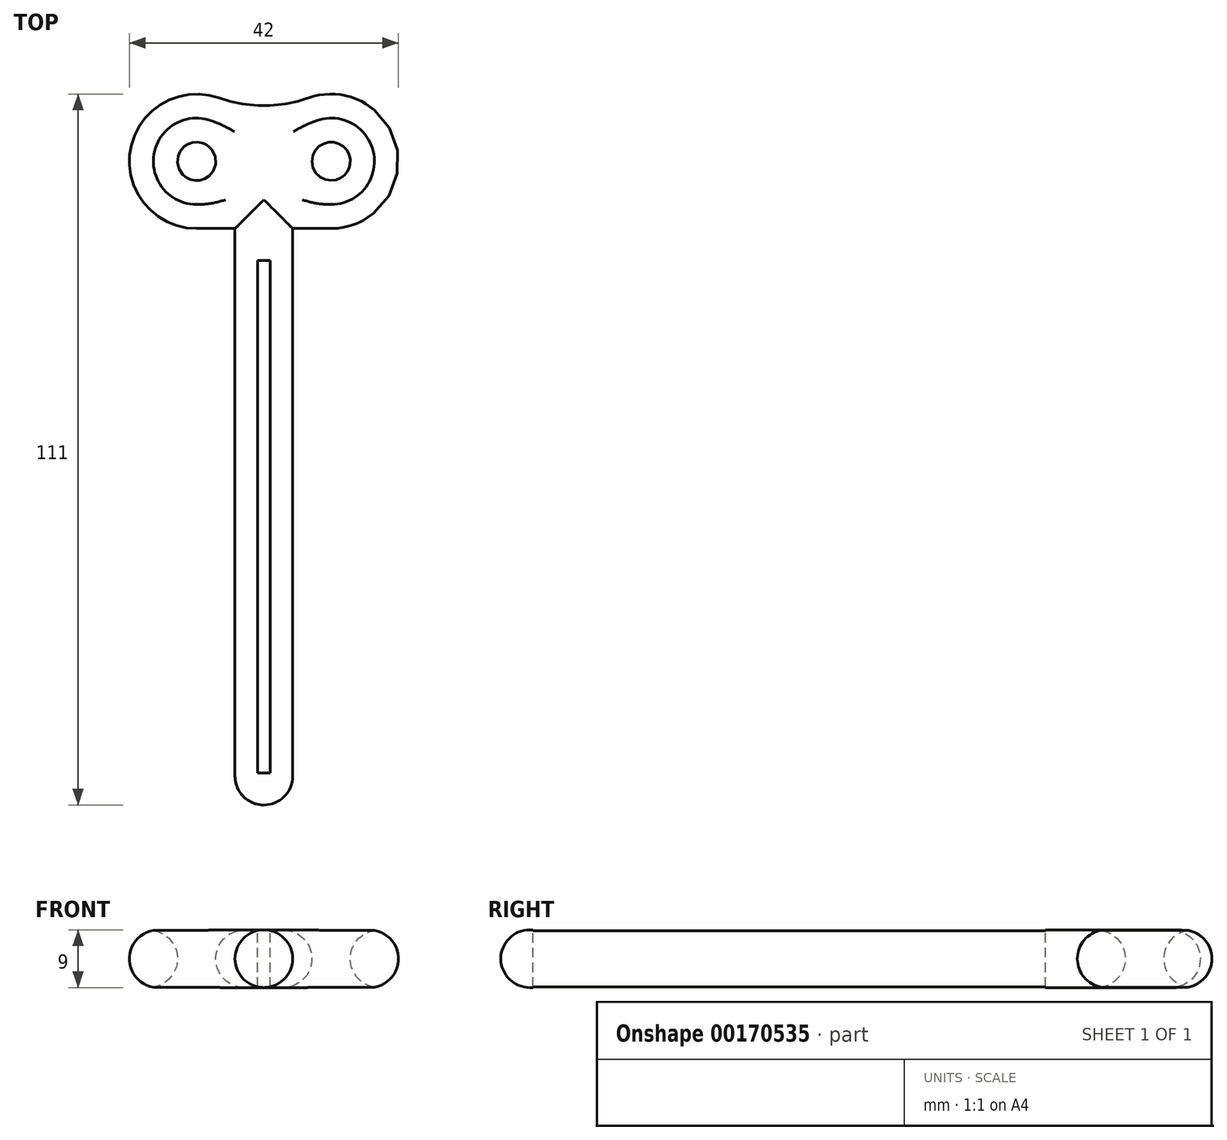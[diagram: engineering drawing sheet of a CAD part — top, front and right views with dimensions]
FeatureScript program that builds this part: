
annotation { "Feature Type Name" : "Feature", "Feature Type Description" : "" }
export const myFeature = defineFeature(function(context is Context, id is Id, definition is map)
    precondition{}
    {
        {
            var Q0;
            Q0=qCreatedBy(makeId("Top.planeOp"),FACE);
            var sketch = newSketch(context, id + "F0", { "sketchPlane" : qUnion([Q0])});
            skLineSegment(sketch, "E0", {"start": v(-4.5, 4.5) * mm, "end": v(-4.5, 90) * mm});
            skLineSegment(sketch, "E1", {"start": v(0, 0) * mm, "end": v(0, 45.82) * mm, "construction": true});
            skArc(sketch, "E2", {"start": v(-4.5, 4.5) * mm, "mid": v(-3.18, 1.32) * mm, "end": v(0, 0) * mm});
            skLineSegment(sketch, "E3", {"start": v(-4.5, 90) * mm, "end": v(0, 90) * mm});
            skLineSegment(sketch, "E4", {"start": v(0, 90) * mm, "end": v(0, 0) * mm});
            skSolve(sketch);
        }
        {
            var Q0;
            Q0=makeQuery(id+"F0.imprint","IMPRINT",FACE,{"disambiguationData":[TD([[makeQuery(id+"F0.imprint","IMPRINT",EDGE,{"derivedFrom":sQuery(id+"F0.wireOp",EDGE,"E0")}),-1.0]])]});
            var Q1;
            Q1=sQuery(id+"F0.wireOp",EDGE,"E4");
            revolve(context, id + "F1", {"entities" : qUnion([Q0]), "axis" : qUnion([Q1]), "revolveType" : RevolveType.FULL});
        }
        {
            var Q0;
            Q0=qCreatedBy(makeId("Top.planeOp"),FACE);
            var sketch = newSketch(context, id + "F2", { "sketchPlane" : qUnion([Q0])});
            skLineSegment(sketch, "E5", {"start": v(-10.5, 100.5) * mm, "end": v(10.5, 100.5) * mm, "construction": true});
            skCircle(sketch, "E6", {"center": v(10.5, 100.5) * mm, "radius": 10.5 * mm});
            skCircle(sketch, "E7", {"center": v(-10.5, 100.5) * mm, "radius": 10.5 * mm});
            skCircle(sketch, "E8", {"center": v(-10.5, 100.5) * mm, "radius": 3 * mm});
            skCircle(sketch, "E9", {"center": v(10.5, 100.5) * mm, "radius": 3 * mm});
            skLineSegment(sketch, "E10", {"start": v(-10.5, 90) * mm, "end": v(10.5, 90) * mm});
            skArc(sketch, "E11", {"start": v(-7, 110.4) * mm, "mid": v(0, 109.2) * mm, "end": v(7, 110.4) * mm});
            skLineSegment(sketch, "E12.bottom", {"start": v(-1, 85) * mm, "end": v(1, 85) * mm});
            skLineSegment(sketch, "E12.top", {"start": v(-1, 5) * mm, "end": v(1, 5) * mm});
            skLineSegment(sketch, "E12.left", {"start": v(-1, 85) * mm, "end": v(-1, 5) * mm});
            skLineSegment(sketch, "E12.right", {"start": v(1, 85) * mm, "end": v(1, 5) * mm});
            skSolve(sketch);
        }
        {
            var Q0;
            Q0=makeQuery(id+"F2.imprint","IMPRINT",FACE,{"disambiguationData":[TD([[makeQuery(id+"F2.imprint","IMPRINT",EDGE,{"derivedFrom":sQuery(id+"F2.wireOp",EDGE,"E8")}),-1.0]])]});
            var Q1;
            {var subQ0=sQuery(id+"F2.wireOp",EDGE,"E10");Q1=makeQuery(id+"F2.imprint","IMPRINT",FACE,{"disambiguationData":[TD([[makeQuery(id+"F2.imprint","IMPRINT",EDGE,{"derivedFrom":subQ0}),1.0]])]});}
            var Q2;
            Q2=makeQuery(id+"F2.imprint","IMPRINT",FACE,{"disambiguationData":[TD([[makeQuery(id+"F2.imprint","IMPRINT",EDGE,{"derivedFrom":sQuery(id+"F2.wireOp",EDGE,"E9")}),-1.0]])]});
            var Q3;
            {var subQ0=sQuery(id+"F2.wireOp",EDGE,"E11");Q3=makeQuery(id+"F2.imprint","IMPRINT",FACE,{"disambiguationData":[TD([[makeQuery(id+"F2.imprint","IMPRINT",EDGE,{"derivedFrom":subQ0}),-1.0]])]});}
            extrude(context, id + "F3", {"entities" : qUnion([Q0, Q1, Q2, Q3]), "operationType" : NewBodyOperationType.ADD, "endBound" : BoundingType.SYMMETRIC, "depth" : 9 * mm});
        }
        {
            var Q0;
            Q0=makeQuery(id+"F2.imprint","IMPRINT",FACE,{"disambiguationData":[TD([[makeQuery(id+"F2.imprint","IMPRINT",EDGE,{"derivedFrom":sQuery(id+"F2.wireOp",EDGE,"E12.bottom")}),-1.0]])]});
            extrude(context, id + "F4", {"entities" : qUnion([Q0]), "operationType" : NewBodyOperationType.REMOVE, "endBound" : BoundingType.SYMMETRIC, "oppositeDirection" : true, "depth" : 25 * mm});
        }
        {
            var Q0;
            Q0=makeQuery(id+"F3.opExtrude","CAP_FACE",FACE,{"disambiguationData":[OSD([sQuery(id+"F2.wireOp",EDGE,"E6"),sQuery(id+"F2.wireOp",EDGE,"E7"),sQuery(id+"F2.wireOp",EDGE,"E8"),sQuery(id+"F2.wireOp",EDGE,"E9"),sQuery(id+"F2.wireOp",EDGE,"E10"),sQuery(id+"F2.wireOp",EDGE,"E11")])],"isStart":true});
            var Q1;
            Q1=makeQuery(id+"F3.opExtrude","CAP_FACE",FACE,{"disambiguationData":[OSD([sQuery(id+"F2.wireOp",EDGE,"E6"),sQuery(id+"F2.wireOp",EDGE,"E7"),sQuery(id+"F2.wireOp",EDGE,"E8"),sQuery(id+"F2.wireOp",EDGE,"E9"),sQuery(id+"F2.wireOp",EDGE,"E10"),sQuery(id+"F2.wireOp",EDGE,"E11")])],"isStart":false});
            fillet(context, id + "F5", {"entities" : qUnion([Q0, Q1]), "radius" : 4.5 * mm, "tangentPropagation" : true, "allowEdgeOverflow" : false});
        }
    });
